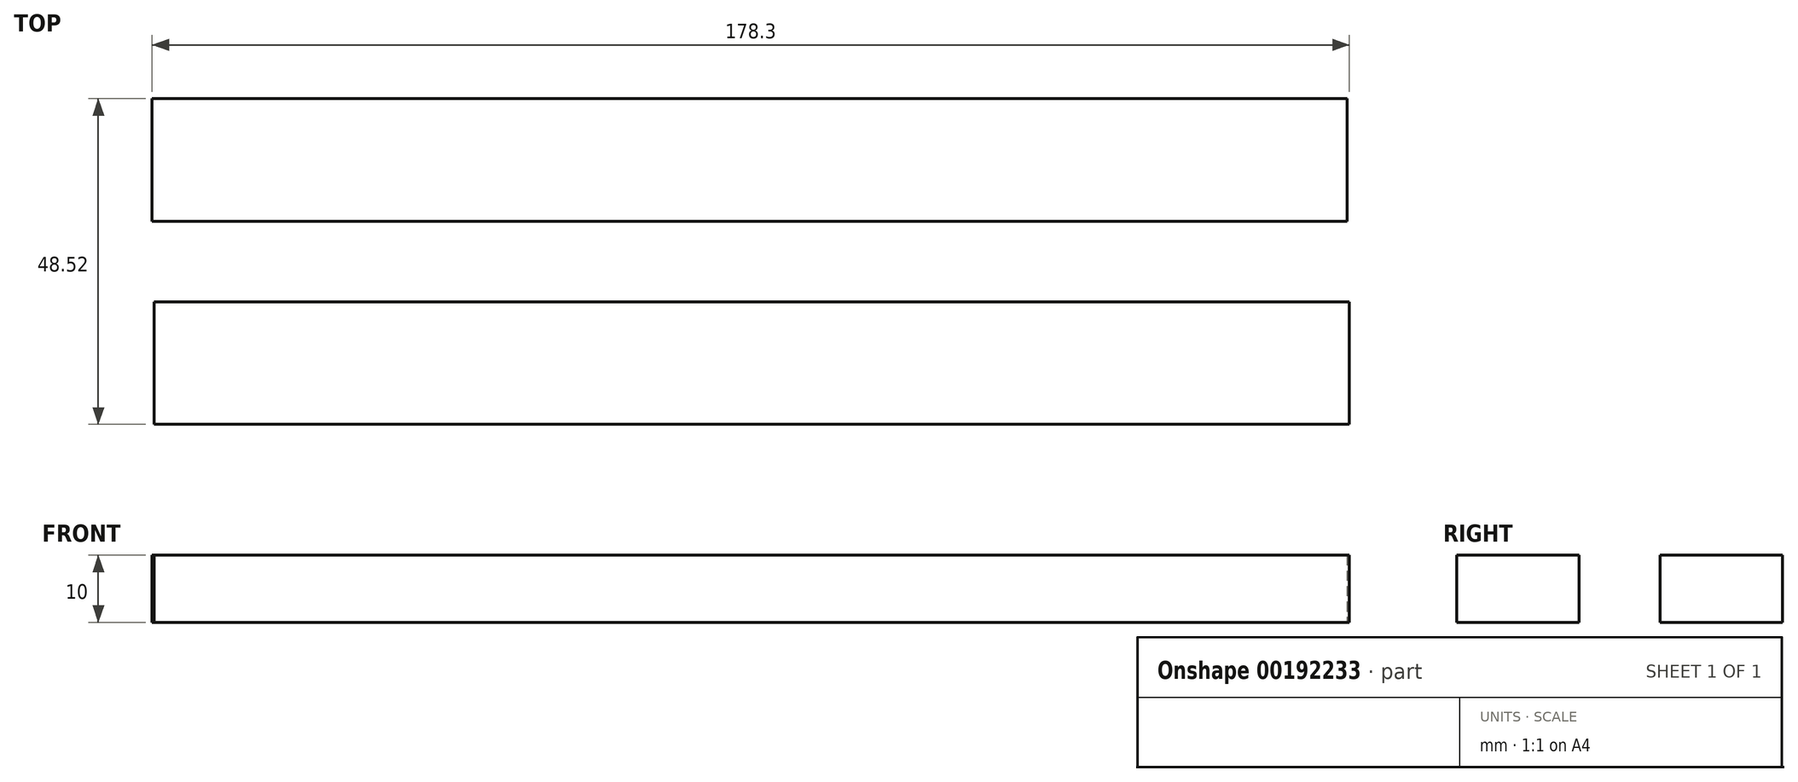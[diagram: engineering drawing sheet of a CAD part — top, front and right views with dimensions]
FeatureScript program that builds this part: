
annotation { "Feature Type Name" : "Feature", "Feature Type Description" : "" }
export const myFeature = defineFeature(function(context is Context, id is Id, definition is map)
    precondition{}
    {
        {
            var Q0;
            Q0=qCreatedBy(makeId("Top.planeOp"),FACE);
            var sketch = newSketch(context, id + "F0", { "sketchPlane" : qUnion([Q0])});
            skLineSegment(sketch, "E0.bottom", {"start": v(89, 9.12) * mm, "end": v(-89, 9.12) * mm});
            skLineSegment(sketch, "E0.top", {"start": v(89, -9.12) * mm, "end": v(-89, -9.12) * mm});
            skLineSegment(sketch, "E0.left", {"start": v(89, 9.12) * mm, "end": v(89, -9.12) * mm});
            skLineSegment(sketch, "E0.right", {"start": v(-89, 9.12) * mm, "end": v(-89, -9.12) * mm});
            skPoint(sketch, "E0.middle", {"position": v(0, 0) * mm});
            skLineSegment(sketch, "E1.1.0.0", {"start": v(88.7, 39.4) * mm, "end": v(-89.3, 39.4) * mm});
            skLineSegment(sketch, "E1.1.0.1", {"start": v(-89.3, 39.4) * mm, "end": v(-89.3, 21.15) * mm});
            skLineSegment(sketch, "E1.1.0.2", {"start": v(88.7, 21.15) * mm, "end": v(-89.3, 21.15) * mm});
            skLineSegment(sketch, "E1.1.0.3", {"start": v(88.7, 39.4) * mm, "end": v(88.7, 21.15) * mm});
            skLineSegment(sketch, "E1.direction1", {"start": v(-89, 9.12) * mm, "end": v(-89.3, 39.4) * mm, "construction": true});
            skSolve(sketch);
        }
        {
            var Q0;
            Q0 = qSketchRegion(id + "F0", true);
            extrude(context, id + "F1", {"entities" : qUnion([Q0]), "depth" : 10 * mm});
        }
    });
